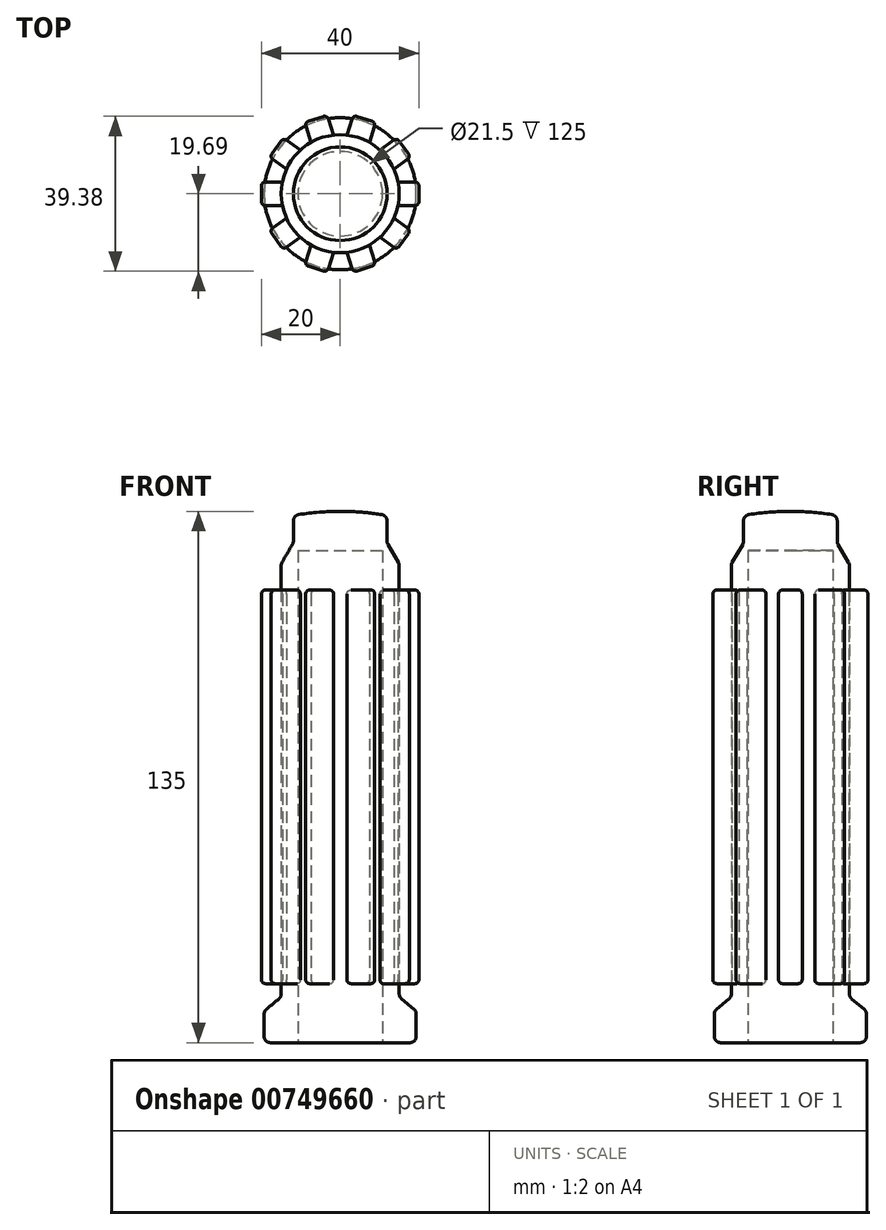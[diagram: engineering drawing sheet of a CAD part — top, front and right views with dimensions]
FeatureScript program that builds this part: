
annotation { "Feature Type Name" : "Feature", "Feature Type Description" : "" }
export const myFeature = defineFeature(function(context is Context, id is Id, definition is map)
    precondition{}
    {
        {
            var Q0;
            Q0=qCreatedBy(makeId("Front.planeOp"),FACE);
            var sketch = newSketch(context, id + "F0", { "sketchPlane" : qUnion([Q0])});
            skLineSegment(sketch, "E0", {"start": v(10.75, 0) * mm, "end": v(19.32, 0) * mm});
            skLineSegment(sketch, "E1", {"start": v(10.75, 0) * mm, "end": v(10.75, 125) * mm});
            skLineSegment(sketch, "E2", {"start": v(10.75, 125) * mm, "end": v(0, 125) * mm});
            skLineSegment(sketch, "E3", {"start": v(0, 125) * mm, "end": v(0, 135) * mm});
            skLineSegment(sketch, "E4", {"start": v(19.32, 0) * mm, "end": v(19.32, 8) * mm});
            skLineSegment(sketch, "E5", {"start": v(19.32, 8) * mm, "end": v(15, 11.63) * mm});
            skLineSegment(sketch, "E6", {"start": v(15, 11.63) * mm, "end": v(15, 121.63) * mm});
            skLineSegment(sketch, "E7", {"start": v(15, 121.63) * mm, "end": v(11.9, 127) * mm});
            skLineSegment(sketch, "E8", {"start": v(11.9, 127) * mm, "end": v(11.9, 133.95) * mm});
            skArc(sketch, "E9", {"start": v(11.9, 133.95) * mm, "mid": v(5.97, 134.74) * mm, "end": v(0, 135) * mm});
            skLineSegment(sketch, "E10", {"start": v(-19.32, 0) * mm, "end": v(19.32, 0) * mm});
            skLineSegment(sketch, "E11", {"start": v(0, 0) * mm, "end": v(0, 135) * mm, "construction": true});
            skSolve(sketch);
        }
        {
            var Q0;
            Q0=makeQuery(id+"F0.imprint","IMPRINT",FACE,{"disambiguationData":[TD([[makeQuery(id+"F0.imprint","IMPRINT",EDGE,{"derivedFrom":sQuery(id+"F0.wireOp",EDGE,"E0")}),1.0]])]});
            var Q1;
            Q1=sQuery(id+"F0.wireOp",EDGE,"E11");
            revolve(context, id + "F1", {"entities" : qUnion([Q0]), "axis" : qUnion([Q1]), "revolveType" : RevolveType.FULL});
        }
        {
            var Q0;
            Q0=makeQuery(id+"F1.opRevolve","SWEPT_FACE",FACE,{"disambiguationData":[OSD([sQuery(id+"F0.wireOp",EDGE,"E4")])]});
            var Q1;
            Q1=makeQuery(id+"F1.opRevolve","SWEPT_EDGE",EDGE,{"disambiguationData":[OSD([sQuery(id+"F0.wireOp",EDGE,"E5"),sQuery(id+"F0.wireOp",EDGE,"E6")])]});
            var Q2;
            Q2=makeQuery(id+"F1.opRevolve","SWEPT_EDGE",EDGE,{"disambiguationData":[OSD([sQuery(id+"F0.wireOp",EDGE,"E6"),sQuery(id+"F0.wireOp",EDGE,"E7")])]});
            var Q3;
            Q3=makeQuery(id+"F1.opRevolve","SWEPT_EDGE",EDGE,{"disambiguationData":[OSD([sQuery(id+"F0.wireOp",EDGE,"E7"),sQuery(id+"F0.wireOp",EDGE,"E8")])]});
            var Q4;
            Q4=makeQuery(id+"F1.opRevolve","SWEPT_EDGE",EDGE,{"disambiguationData":[OSD([sQuery(id+"F0.wireOp",EDGE,"E8"),sQuery(id+"F0.wireOp",EDGE,"E9")])]});
            fillet(context, id + "F2", {"entities" : qUnion([Q0, Q1, Q2, Q3, Q4]), "radius" : 1.6 * mm, "tangentPropagation" : true, "allowEdgeOverflow" : false});
        }
        {
            var Q0;
            Q0=qCreatedBy(makeId("Right.planeOp"),FACE);
            cPlane(context, id + "F3", {"entities" : qUnion([Q0]), "cplaneType" : CPlaneType.OFFSET, "offset" : 20 * mm, "width" : 150 * mm, "height" : 150 * mm});
        }
        {
            var Q0;
            Q0=qCreatedBy(id+"F3.planeOp",FACE);
            var sketch = newSketch(context, id + "F4", { "sketchPlane" : qUnion([Q0])});
            skLineSegment(sketch, "E12.bottom", {"start": v(-3, 15) * mm, "end": v(3, 15) * mm});
            skLineSegment(sketch, "E12.top", {"start": v(-3, 115) * mm, "end": v(3, 115) * mm});
            skLineSegment(sketch, "E12.left", {"start": v(-3, 15) * mm, "end": v(-3, 115) * mm});
            skLineSegment(sketch, "E12.right", {"start": v(3, 15) * mm, "end": v(3, 115) * mm});
            skSolve(sketch);
        }
        {
            var Q0;
            Q0=qSketchRegion(id+"F4",true);
            var Q1;
            Q1=makeQuery(id+"F1.opRevolve","SWEPT_FACE",FACE,{"disambiguationData":[OSD([sQuery(id+"F0.wireOp",EDGE,"E6")])]});
            extrude(context, id + "F5", {"entities" : qUnion([Q0]), "endBound" : BoundingType.UP_TO_SURFACE, "oppositeDirection" : true, "depth" : 25 * mm, "endBoundEntityFace" : qUnion([Q1]), "offsetDistance" : 25 * mm});
        }
        {
            var Q0;
            Q0=makeQuery(id+"F5.opExtrude","SWEPT_EDGE",EDGE,{"disambiguationData":[OSD([sQuery(id+"F4.wireOp",EDGE,"E12.bottom"),sQuery(id+"F4.wireOp",EDGE,"E12.left")])]});
            var Q1;
            Q1=makeQuery(id+"F5.opExtrude","CAP_EDGE",EDGE,{"disambiguationData":[OSD([sQuery(id+"F4.wireOp",EDGE,"E12.bottom")])],"isStart":true});
            var Q2;
            Q2=makeQuery(id+"F5.opExtrude","SWEPT_EDGE",EDGE,{"disambiguationData":[OSD([sQuery(id+"F4.wireOp",EDGE,"E12.bottom"),sQuery(id+"F4.wireOp",EDGE,"E12.right")])]});
            var Q3;
            Q3=makeQuery(id+"F5.opExtrude","CAP_EDGE",EDGE,{"disambiguationData":[OSD([sQuery(id+"F4.wireOp",EDGE,"E12.right")])],"isStart":true});
            var Q4;
            Q4=makeQuery(id+"F5.opExtrude","CAP_EDGE",EDGE,{"disambiguationData":[OSD([sQuery(id+"F4.wireOp",EDGE,"E12.left")])],"isStart":true});
            var Q5;
            Q5=makeQuery(id+"F5.opExtrude","SWEPT_EDGE",EDGE,{"disambiguationData":[OSD([sQuery(id+"F4.wireOp",EDGE,"E12.top"),sQuery(id+"F4.wireOp",EDGE,"E12.left")])]});
            var Q6;
            Q6=makeQuery(id+"F5.opExtrude","CAP_EDGE",EDGE,{"disambiguationData":[OSD([sQuery(id+"F4.wireOp",EDGE,"E12.top")])],"isStart":true});
            var Q7;
            Q7=makeQuery(id+"F5.opExtrude","SWEPT_EDGE",EDGE,{"disambiguationData":[OSD([sQuery(id+"F4.wireOp",EDGE,"E12.top"),sQuery(id+"F4.wireOp",EDGE,"E12.right")])]});
            fillet(context, id + "F6", {"entities" : qUnion([Q0, Q1, Q2, Q3, Q4, Q5, Q6, Q7]), "radius" : 1 * mm, "tangentPropagation" : true, "allowEdgeOverflow" : false});
        }
        {
            var Q0;
            Q0=makeQuery(id+"F5.opExtrude","SWEPT_BODY",BODY,{"disambiguationData":[OSD([sQuery(id+"F4.wireOp",EDGE,"E12.bottom"),sQuery(id+"F4.wireOp",EDGE,"E12.top"),sQuery(id+"F4.wireOp",EDGE,"E12.left"),sQuery(id+"F4.wireOp",EDGE,"E12.right")])]});
            var Q1;
            Q1=sQuery(id+"F0.wireOp",EDGE,"E11");
            circularPattern(context, id + "F7", {"entities" : qUnion([Q0]), "axis" : qUnion([Q1]), "angle" : 360 * degree, "instanceCount" : 10, "equalSpace" : true});
        }
    });
